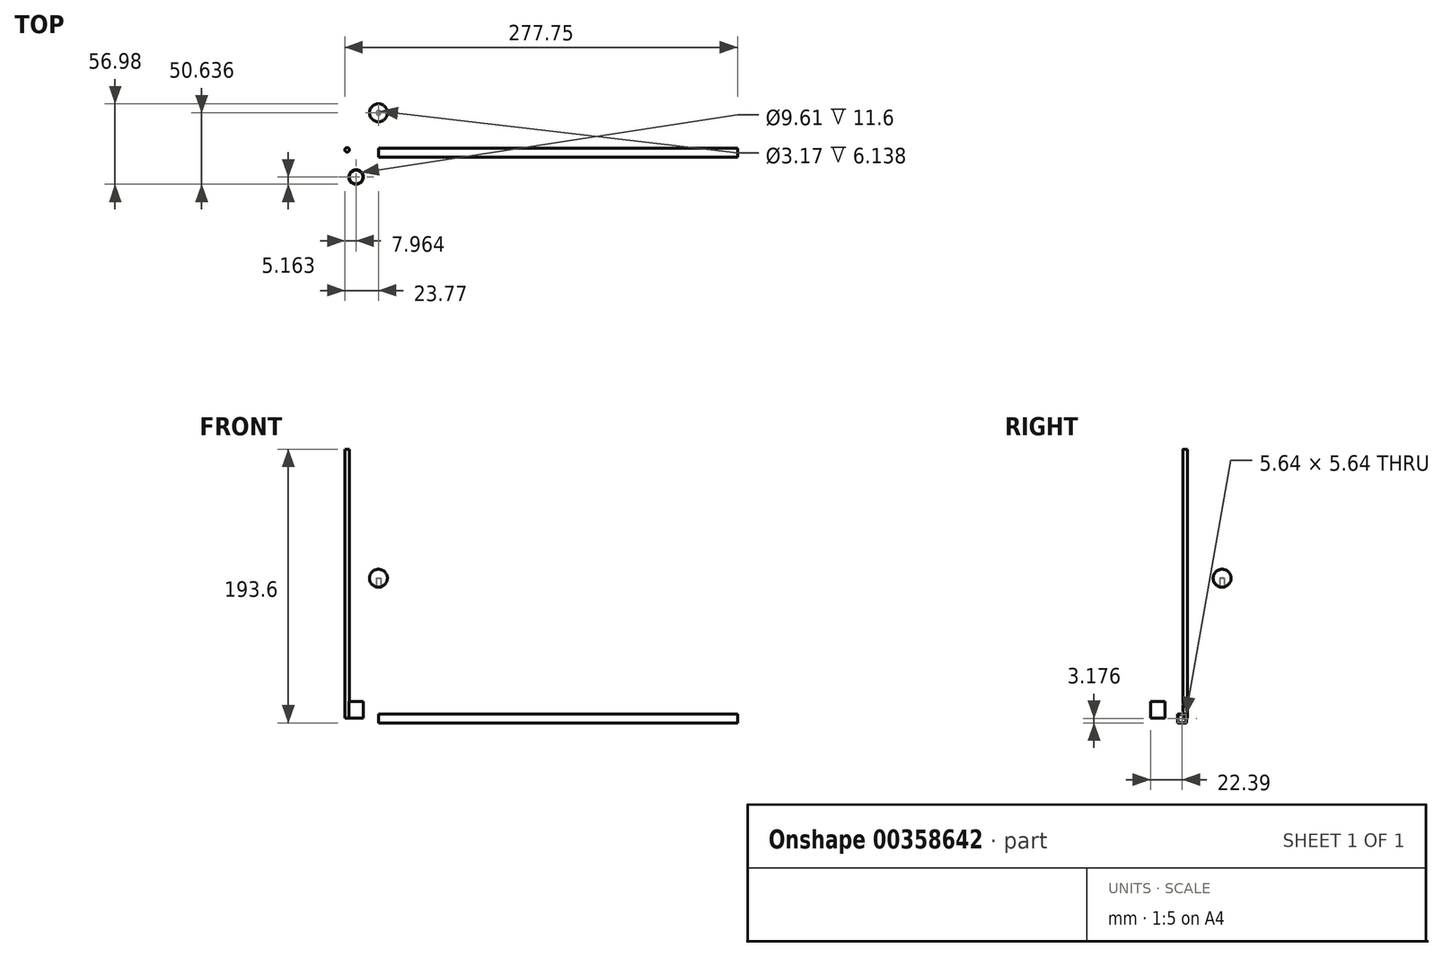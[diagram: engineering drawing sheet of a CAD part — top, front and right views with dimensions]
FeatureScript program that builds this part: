
annotation { "Feature Type Name" : "Feature", "Feature Type Description" : "" }
export const myFeature = defineFeature(function(context is Context, id is Id, definition is map)
    precondition{}
    {
        {
            assignVariable(context, id + "F0", {"name" : "Rod", "anyValue" : 212.9 - 22.78});
        }
        {
            assignVariable(context, id + "F1", {"name" : "Tube", "anyValue" : 253.98});
        }
        {
            var Q0;
            Q0=qCreatedBy(makeId("Right.planeOp"),FACE);
            var sketch = newSketch(context, id + "F2", { "sketchPlane" : qUnion([Q0])});
            skArc(sketch, "E0", {"start": v(28.59, 105.28) * mm, "mid": v(22.3, 99.74) * mm, "end": v(27, 92.8) * mm});
            skLineSegment(sketch, "E1", {"start": v(28.59, 98.94) * mm, "end": v(28.59, 105.28) * mm});
            skLineSegment(sketch, "E2", {"start": v(28.59, 98.94) * mm, "end": v(27, 98.94) * mm});
            skLineSegment(sketch, "E3", {"start": v(27, 98.94) * mm, "end": v(27, 92.8) * mm});
            skSolve(sketch);
        }
        {
            var Q0;
            Q0=makeQuery(id+"F2.imprint","IMPRINT",FACE,{"disambiguationData":[TD([[makeQuery(id+"F2.imprint","IMPRINT",EDGE,{"derivedFrom":sQuery(id+"F2.wireOp",EDGE,"E0")}),1.0]])]});
            var Q1;
            Q1=sQuery(id+"F2.wireOp",EDGE,"E1");
            revolve(context, id + "F3", {"entities" : qUnion([Q0]), "axis" : qUnion([Q1]), "revolveType" : RevolveType.FULL});
        }
        {
            var Q0;
            Q0=qCreatedBy(makeId("Right.planeOp"),FACE);
            var sketch = newSketch(context, id + "F4", { "sketchPlane" : qUnion([Q0])});
            skLineSegment(sketch, "E4.bottom", {"start": v(-2.84, 2.87) * mm, "end": v(3.51, 2.87) * mm});
            skLineSegment(sketch, "E4.top", {"start": v(-2.84, -3.48) * mm, "end": v(3.51, -3.48) * mm});
            skLineSegment(sketch, "E4.left", {"start": v(-2.84, 2.87) * mm, "end": v(-2.84, -3.48) * mm});
            skLineSegment(sketch, "E4.right", {"start": v(3.51, 2.87) * mm, "end": v(3.51, -3.48) * mm});
            skLineSegment(sketch, "E5.bottom", {"start": v(-2.48, 2.52) * mm, "end": v(3.16, 2.52) * mm});
            skLineSegment(sketch, "E5.top", {"start": v(-2.48, -3.12) * mm, "end": v(3.16, -3.12) * mm});
            skLineSegment(sketch, "E5.left", {"start": v(-2.48, 2.52) * mm, "end": v(-2.48, -3.12) * mm});
            skLineSegment(sketch, "E5.right", {"start": v(3.16, 2.52) * mm, "end": v(3.16, -3.12) * mm});
            skSolve(sketch);
        }
        {
            var Q0;
            Q0=makeQuery(id+"F4.imprint","IMPRINT",FACE,{"disambiguationData":[TD([[makeQuery(id+"F4.imprint","IMPRINT",EDGE,{"derivedFrom":sQuery(id+"F4.wireOp",EDGE,"E4.bottom")}),-1.0]])]});
            extrude(context, id + "F5", {"entities" : qUnion([Q0]), "depth" : (getVariable(context, 'Tube')) * mm, "offsetDistance" : 25 * mm});
        }
        {
            var Q0;
            Q0=qCreatedBy(makeId("Top.planeOp"),FACE);
            var sketch = newSketch(context, id + "F6", { "sketchPlane" : qUnion([Q0])});
            skCircle(sketch, "E6", {"center": v(-22.19, 2.38) * mm, "radius": 1.59 * mm});
            skSolve(sketch);
        }
        {
            var Q0;
            Q0=makeQuery(id+"F6.imprint","IMPRINT",FACE,{"disambiguationData":[TD([[makeQuery(id+"F6.imprint","IMPRINT",EDGE,{"derivedFrom":sQuery(id+"F6.wireOp",EDGE,"E6")}),1.0]])]});
            extrude(context, id + "F7", {"entities" : qUnion([Q0]), "depth" : (getVariable(context, 'Rod')) * mm, "offsetDistance" : 25 * mm});
        }
        {
            var Q0;
            Q0=qCreatedBy(makeId("Top.planeOp"),FACE);
            var sketch = newSketch(context, id + "F8", { "sketchPlane" : qUnion([Q0])});
            skCircle(sketch, "E7", {"center": v(-15.8, -16.89) * mm, "radius": 4.8 * mm});
            skCircle(sketch, "E8", {"center": v(-15.8, -16.89) * mm, "radius": 5.16 * mm});
            skSolve(sketch);
        }
        {
            var Q0;
            Q0=makeQuery(id+"F8.imprint","IMPRINT",FACE,{"disambiguationData":[TD([[makeQuery(id+"F8.imprint","IMPRINT",EDGE,{"derivedFrom":sQuery(id+"F8.wireOp",EDGE,"E7")}),-1.0]])]});
            extrude(context, id + "F9", {"entities" : qUnion([Q0]), "depth" : 11.6 * mm, "offsetDistance" : 25 * mm});
        }
    });
